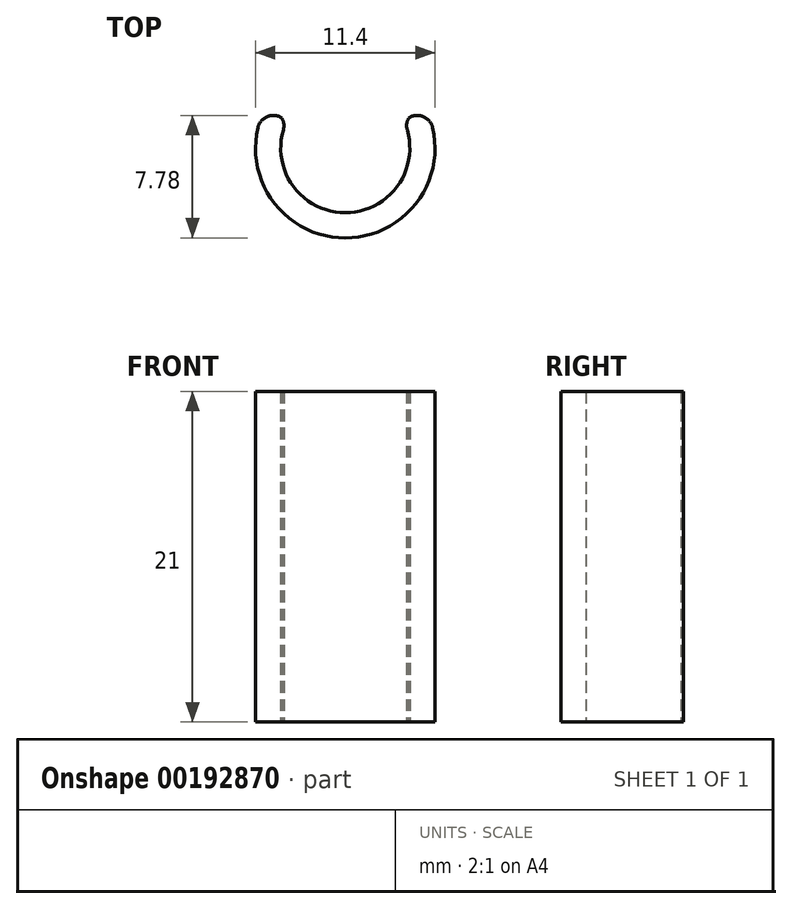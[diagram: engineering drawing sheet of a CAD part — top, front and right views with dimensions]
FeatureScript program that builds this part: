
annotation { "Feature Type Name" : "Feature", "Feature Type Description" : "" }
export const myFeature = defineFeature(function(context is Context, id is Id, definition is map)
    precondition{}
    {
        {
            var Q0;
            Q0=qCreatedBy(makeId("Top.planeOp"),FACE);
            var sketch = newSketch(context, id + "F0", { "sketchPlane" : qUnion([Q0])});
            skCircle(sketch, "E0", {"center": v(0, 0) * mm, "radius": 4.1 * mm});
            skCircle(sketch, "E1.0", {"center": v(0, 0) * mm, "radius": 5.7 * mm});
            skLineSegment(sketch, "E2", {"start": v(0, 0) * mm, "end": v(0, 5.7) * mm, "construction": true});
            skCircle(sketch, "E3", {"center": v(0, 5.7) * mm, "radius": 5.5 * mm});
            skSolve(sketch);
        }
        {
            var Q0;
            {var subQ0=sQuery(id+"F0.wireOp",EDGE,"E3");var subQ1=sQuery(id+"F0.wireOp",EDGE,"E0");var subQ2=makeQuery(id+"F0.imprint","INTERSECT",VERTEX,{"disambiguationData":[OD(0.0)],"derivedFrom":[subQ1,subQ0]});Q0=makeQuery(id+"F0.imprint","IMPRINT",FACE,{"disambiguationData":[TD([[makeQuery(id+"F0.imprint","IMPRINT",EDGE,{"disambiguationData":[TD([[subQ2,-1.0]])],"derivedFrom":subQ1}),-1.0]])]});}
            extrude(context, id + "F1", {"entities" : qUnion([Q0]), "depth" : 21 * mm});
        }
        {
            var Q0;
            {var subQ0=sQuery(id+"F0.wireOp",EDGE,"E3");var subQ1=sQuery(id+"F0.wireOp",EDGE,"E0");Q0=makeQuery(id+"F1.opExtrude","SWEPT_EDGE",EDGE,{"disambiguationData":[OSD([subQ1,subQ0]),TDD([makeQuery(id+"F0.imprint","INTERSECT",VERTEX,{"disambiguationData":[OD(1.0)],"derivedFrom":[subQ1,subQ0]})])]});}
            var Q1;
            {var subQ0=sQuery(id+"F0.wireOp",EDGE,"E3");var subQ1=sQuery(id+"F0.wireOp",EDGE,"E1.0");Q1=makeQuery(id+"F1.opExtrude","SWEPT_EDGE",EDGE,{"disambiguationData":[OSD([subQ1,subQ0]),TDD([makeQuery(id+"F0.imprint","INTERSECT",VERTEX,{"disambiguationData":[OD(1.0)],"derivedFrom":[subQ1,subQ0]})])]});}
            var Q2;
            {var subQ0=sQuery(id+"F0.wireOp",EDGE,"E3");var subQ1=sQuery(id+"F0.wireOp",EDGE,"E0");Q2=makeQuery(id+"F1.opExtrude","SWEPT_EDGE",EDGE,{"disambiguationData":[OSD([subQ1,subQ0]),TDD([makeQuery(id+"F0.imprint","INTERSECT",VERTEX,{"disambiguationData":[OD(0.0)],"derivedFrom":[subQ1,subQ0]})])]});}
            var Q3;
            {var subQ0=sQuery(id+"F0.wireOp",EDGE,"E3");var subQ1=sQuery(id+"F0.wireOp",EDGE,"E1.0");Q3=makeQuery(id+"F1.opExtrude","SWEPT_EDGE",EDGE,{"disambiguationData":[OSD([subQ1,subQ0]),TDD([makeQuery(id+"F0.imprint","INTERSECT",VERTEX,{"disambiguationData":[OD(0.0)],"derivedFrom":[subQ1,subQ0]})])]});}
            fillet(context, id + "F2", {"entities" : qUnion([Q0, Q1, Q2, Q3]), "radius" : 1 * mm, "tangentPropagation" : true, "allowEdgeOverflow" : false});
        }
    });
